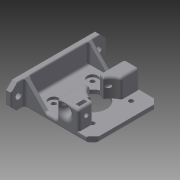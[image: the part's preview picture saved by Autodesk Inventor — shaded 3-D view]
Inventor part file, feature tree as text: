
AUTODESK INVENTOR PART (.ipt)
format: ipt  version: 2014 (Build 180170000, 170)  size: 465,408 bytes
history: native  units: mm
features: other x2, extrude x2, boolean_combine x1, sketch x1, projected_geometry x1
ambient origin geometry x8: Origin, YZ Plane, XZ Plane, XY Plane, X Axis, Y Axis, Z Axis, Center Point
bodies: Solid2 (feature_tree), Solid1 (feature_tree)
feature tree (7):
  other  "bowden-extruder.ipt"
  extrude  "Extrusion1"  Depth=10.0mm TaperAngle=0.0deg
  boolean_combine  "Combine1"
  extrude  "extruder base::bowden-extruder.ipt"  [1 undecoded]
  other  "TaggingFeature1"
  sketch  "Sketch1"  dims[d0=10.0mm d1=6.0mm d2=0.0mm]
  projected_geometry  "Projected Loop1"
note: 1 required parameter value undecoded (feature->parameter linkage not recoverable at this tier; creation-order binding heuristic only, values carry confidence <= 0.55)
